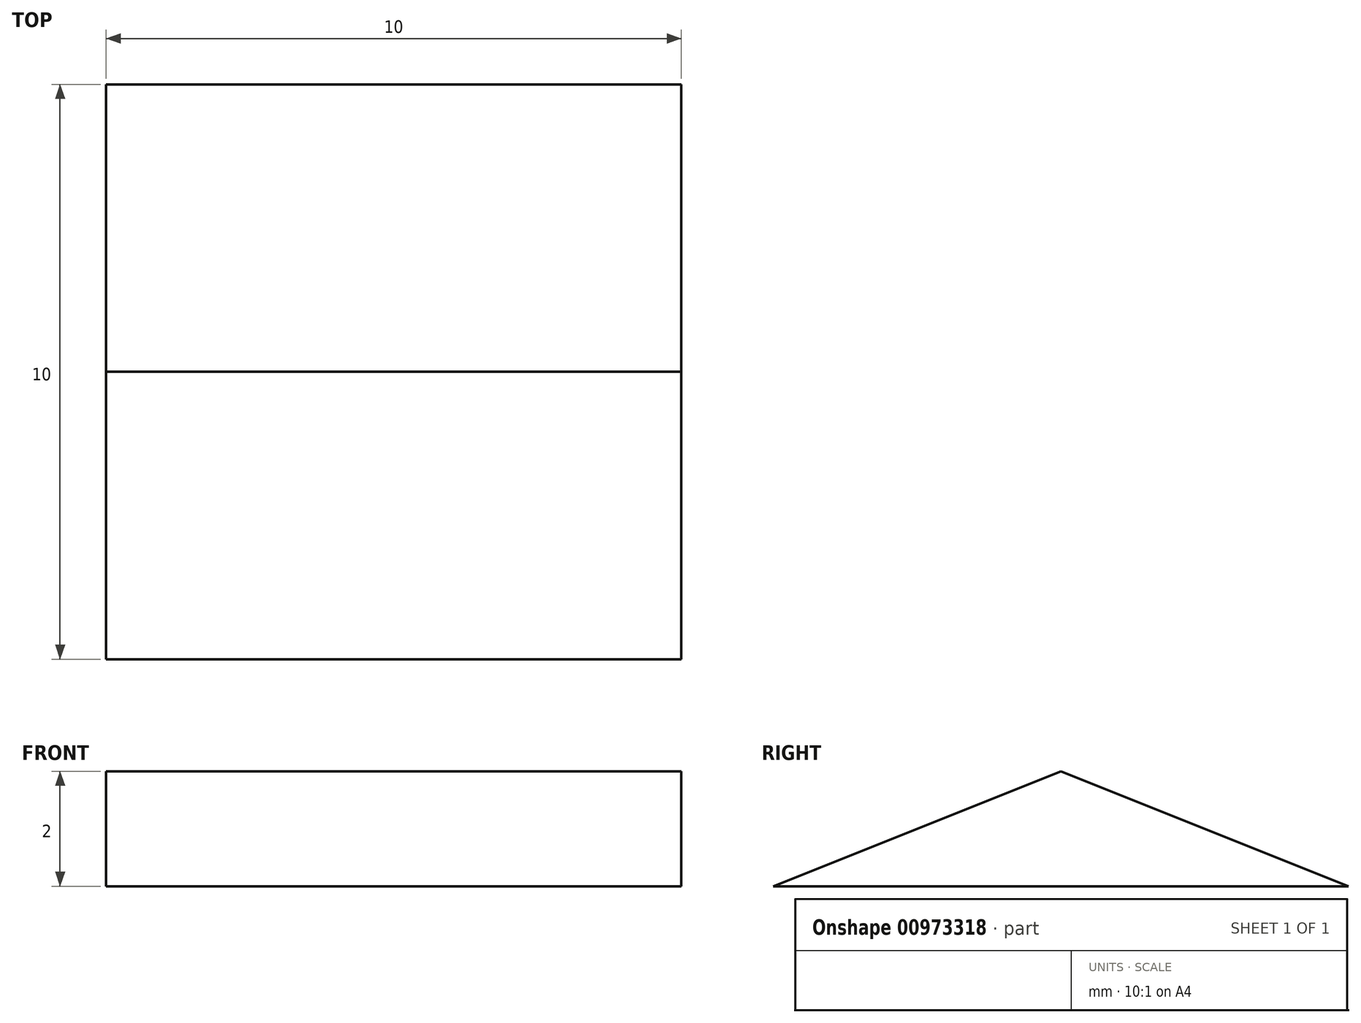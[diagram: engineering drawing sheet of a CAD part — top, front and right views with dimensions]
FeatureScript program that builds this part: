
annotation { "Feature Type Name" : "Feature", "Feature Type Description" : "" }
export const myFeature = defineFeature(function(context is Context, id is Id, definition is map)
    precondition{}
    {
        {
            assignVariable(context, id + "F0", {"name" : "barlength", "anyValue" : 10});
        }
        {
            assignVariable(context, id + "F1", {"name" : "top", "anyValue" : 2});
        }
        {
            assignVariable(context, id + "F2", {"name" : "bottom", "anyValue" : 3});
        }
        {
            var Q0;
            Q0=qCreatedBy(makeId("Top.planeOp"),FACE);
            var sketch = newSketch(context, id + "F3", { "sketchPlane" : qUnion([Q0])});
            skLineSegment(sketch, "E0.bottom", {"start": v(-5, 5) * mm, "end": v(5, 5) * mm});
            skLineSegment(sketch, "E0.top", {"start": v(-5, -5) * mm, "end": v(5, -5) * mm});
            skLineSegment(sketch, "E0.left", {"start": v(-5, 5) * mm, "end": v(-5, -5) * mm});
            skLineSegment(sketch, "E0.right", {"start": v(5, 5) * mm, "end": v(5, -5) * mm});
            skLineSegment(sketch, "E1.bottom", {"start": v(-5, 5) * mm, "end": v(-10, 5) * mm});
            skLineSegment(sketch, "E1.top", {"start": v(-5, -5) * mm, "end": v(-10, -5) * mm});
            skLineSegment(sketch, "E1.right", {"start": v(-10, 5) * mm, "end": v(-10, -5) * mm});
            skLineSegment(sketch, "E2", {"start": v(-10, -5) * mm, "end": v(-10, -6.82) * mm});
            skLineSegment(sketch, "E3", {"start": v(-5, -5) * mm, "end": v(-10, -6.82) * mm});
            skLineSegment(sketch, "E4.MirrorCS", {"start": v(-5, 5) * mm, "end": v(-10, 6.82) * mm});
            skLineSegment(sketch, "E5.MirrorCS", {"start": v(-10, 5) * mm, "end": v(-10, 6.82) * mm});
            skLineSegment(sketch, "E6.MirrorCS", {"start": v(10, 5) * mm, "end": v(10, -5) * mm});
            skLineSegment(sketch, "E7.MirrorCS", {"start": v(5, -5) * mm, "end": v(10, -6.82) * mm});
            skLineSegment(sketch, "E8.MirrorCS", {"start": v(10, -5) * mm, "end": v(10, -6.82) * mm});
            skLineSegment(sketch, "E9.MirrorCS", {"start": v(5, 5) * mm, "end": v(10, 6.82) * mm});
            skLineSegment(sketch, "E10.MirrorCS", {"start": v(10, 5) * mm, "end": v(10, 6.82) * mm});
            skSolve(sketch);
        }
        {
            var Q0;
            Q0=makeQuery(id+"F3.imprint","IMPRINT",FACE,{"disambiguationData":[TD([[makeQuery(id+"F3.imprint","IMPRINT",EDGE,{"derivedFrom":sQuery(id+"F3.wireOp",EDGE,"E0.right")}),1.0]])]});
            var Q1;
            Q1=makeQuery(id+"F3.imprint","IMPRINT",FACE,{"disambiguationData":[TD([[makeQuery(id+"F3.imprint","IMPRINT",EDGE,{"derivedFrom":sQuery(id+"F3.wireOp",EDGE,"E0.bottom")}),-1.0]])]});
            var Q2;
            Q2=makeQuery(id+"F3.imprint","IMPRINT",FACE,{"disambiguationData":[TD([[makeQuery(id+"F3.imprint","IMPRINT",EDGE,{"derivedFrom":sQuery(id+"F3.wireOp",EDGE,"E1.bottom")}),1.0]])]});
            var Q3;
            Q3=makeQuery(id+"F3.imprint","IMPRINT",FACE,{"disambiguationData":[TD([[makeQuery(id+"F3.imprint","IMPRINT",EDGE,{"derivedFrom":sQuery(id+"F3.wireOp",EDGE,"E1.top")}),1.0]])]});
            var Q4;
            Q4=makeQuery(id+"F3.imprint","IMPRINT",FACE,{"disambiguationData":[TD([[makeQuery(id+"F3.imprint","IMPRINT",EDGE,{"derivedFrom":sQuery(id+"F3.wireOp",EDGE,"E1.bottom")}),-1.0]])]});
            extrude(context, id + "F4", {"entities" : qUnion([Q0, Q1, Q2, Q3, Q4]), "depth" : (getVariable(context, 'bottom')) * mm, "offsetDistance" : 25 * mm});
        }
        {
            var Q0;
            Q0=makeQuery(id+"F3.imprint","IMPRINT",FACE,{"disambiguationData":[TD([[makeQuery(id+"F3.imprint","IMPRINT",EDGE,{"derivedFrom":sQuery(id+"F3.wireOp",EDGE,"E0.bottom")}),-1.0]])]});
            extrude(context, id + "F5", {"entities" : qUnion([Q0]), "depth" : (getVariable(context, 'bottom') + getVariable(context, 'top')) * mm, "offsetDistance" : 25 * mm, "hasSecondDirection" : true, "secondDirectionOppositeDirection" : false, "secondDirectionDepth" : (getVariable(context, 'bottom')) * mm});
        }
        {
            var Q0;
            Q0=makeQuery(id+"F5.opExtrude","SWEPT_FACE",FACE,{"disambiguationData":[OSD([sQuery(id+"F3.wireOp",EDGE,"E0.left")])]});
            var sketch = newSketch(context, id + "F6", { "sketchPlane" : qUnion([Q0])});
            skLineSegment(sketch, "E11", {"start": v(0, 5) * mm, "end": v(-5, 3) * mm});
            skLineSegment(sketch, "E12", {"start": v(-5, 3) * mm, "end": v(5, 3) * mm});
            skLineSegment(sketch, "E13", {"start": v(5, 3) * mm, "end": v(0, 5) * mm});
            skSolve(sketch);
        }
        {
            var Q0;
            Q0=makeQuery(id+"F6.imprint","IMPRINT",FACE,{"disambiguationData":[TD([[makeQuery(id+"F6.imprint","IMPRINT",EDGE,{"derivedFrom":sQuery(id+"F6.wireOp",EDGE,"E11")}),1.0]])]});
            extrude(context, id + "F7", {"entities" : qUnion([Q0]), "operationType" : NewBodyOperationType.INTERSECT, "oppositeDirection" : true, "depth" : (getVariable(context, 'barlength')) * mm, "offsetDistance" : 25 * mm});
        }
    });
